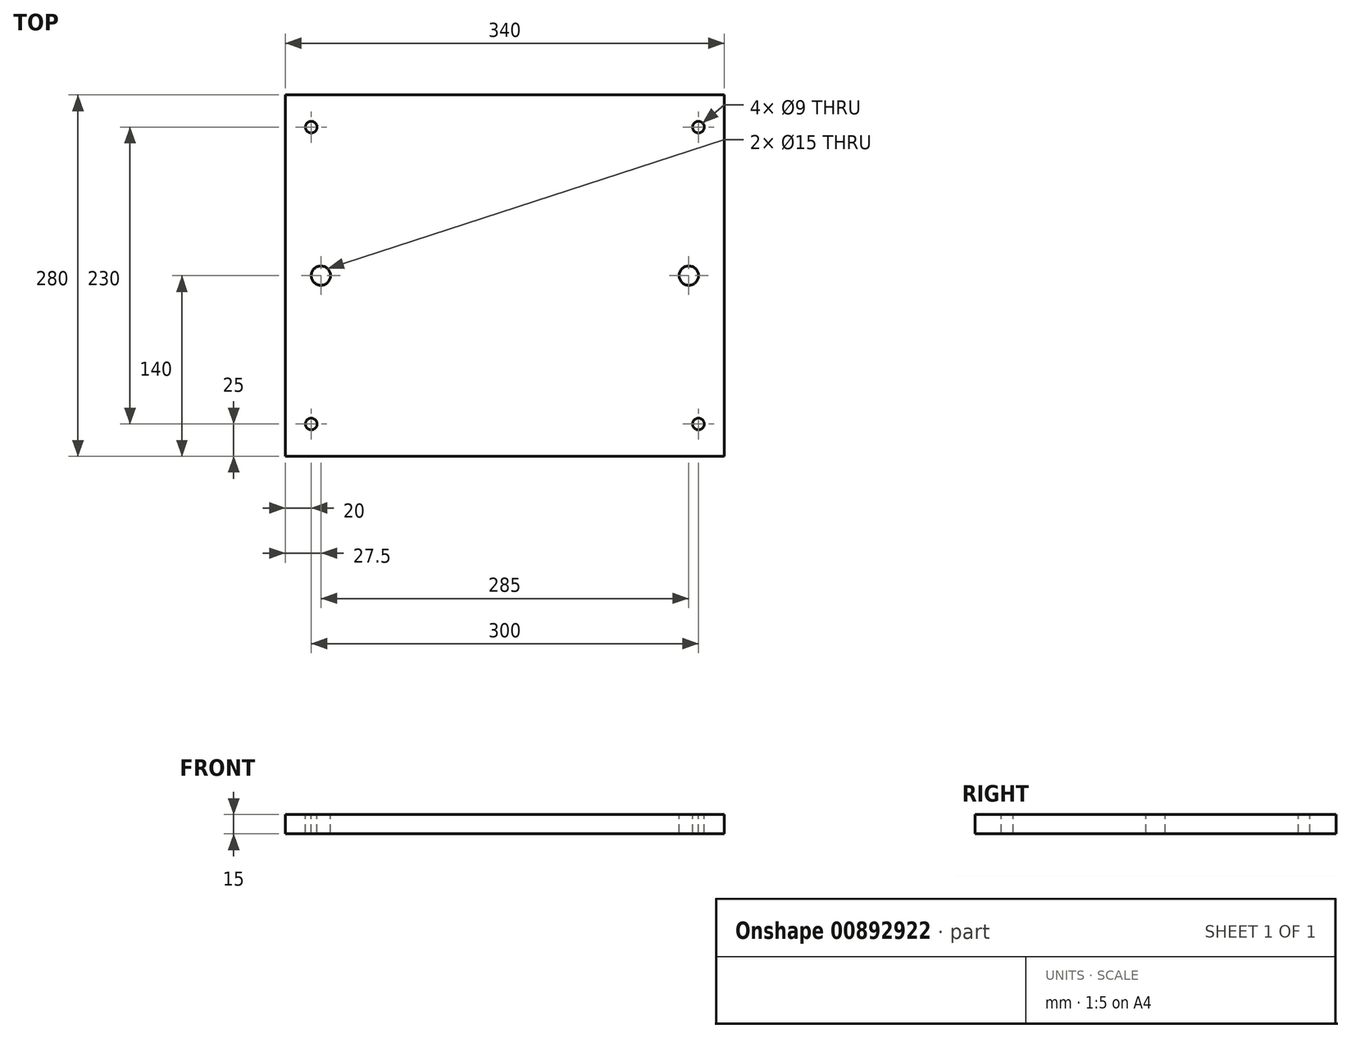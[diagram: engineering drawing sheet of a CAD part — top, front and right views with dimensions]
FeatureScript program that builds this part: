
annotation { "Feature Type Name" : "Feature", "Feature Type Description" : "" }
export const myFeature = defineFeature(function(context is Context, id is Id, definition is map)
    precondition{}
    {
        {
            var Q0;
            Q0=qCreatedBy(makeId("Top.planeOp"),FACE);
            var sketch = newSketch(context, id + "F0", { "sketchPlane" : qUnion([Q0])});
            skLineSegment(sketch, "E0.bottom", {"start": v(-170, 140) * mm, "end": v(170, 140) * mm});
            skLineSegment(sketch, "E0.top", {"start": v(-170, -140) * mm, "end": v(170, -140) * mm});
            skLineSegment(sketch, "E0.left", {"start": v(-170, 140) * mm, "end": v(-170, -140) * mm});
            skLineSegment(sketch, "E0.right", {"start": v(170, 140) * mm, "end": v(170, -140) * mm});
            skSolve(sketch);
        }
        {
            var Q0;
            Q0 = qSketchRegion(id + "F0", true);
            extrude(context, id + "F1", {"entities" : qUnion([Q0]), "depth" : 15 * mm, "offsetDistance" : 25 * mm});
        }
        {
            var Q0;
            Q0=makeQuery(id+"F1.opExtrude","CAP_FACE",FACE,{"disambiguationData":[OSD([sQuery(id+"F0.wireOp",EDGE,"E0.bottom"),sQuery(id+"F0.wireOp",EDGE,"E0.top"),sQuery(id+"F0.wireOp",EDGE,"E0.left"),sQuery(id+"F0.wireOp",EDGE,"E0.right")])],"isStart":false});
            var sketch = newSketch(context, id + "F2", { "sketchPlane" : qUnion([Q0])});
            skLineSegment(sketch, "E1", {"start": v(0, 140) * mm, "end": v(0, -140) * mm, "construction": true});
            skLineSegment(sketch, "E2", {"start": v(-170, 57.5) * mm, "end": v(170, 57.5) * mm, "construction": true});
            skLineSegment(sketch, "E3", {"start": v(-170, -57.5) * mm, "end": v(170, -57.5) * mm, "construction": true});
            skLineSegment(sketch, "E4", {"start": v(-150, 140) * mm, "end": v(-150, -140) * mm, "construction": true});
            skLineSegment(sketch, "E5", {"start": v(150, 140) * mm, "end": v(150, -140) * mm, "construction": true});
            skPoint(sketch, "E6", {"position": v(-150, -115) * mm});
            skPoint(sketch, "E7", {"position": v(-150, 115) * mm});
            skLineSegment(sketch, "E8", {"start": v(142.5, 0) * mm, "end": v(-142.5, 0) * mm, "construction": true});
            skPoint(sketch, "E9.MirrorP", {"position": v(150, -115) * mm});
            skPoint(sketch, "E10.MirrorP", {"position": v(150, 115) * mm});
            skPoint(sketch, "E11", {"position": v(-142.5, 0) * mm});
            skPoint(sketch, "E12", {"position": v(142.5, 0) * mm});
            skPoint(sketch, "E13", {"position": v(-150, 0) * mm});
            skSolve(sketch);
        }
        {
            var Q0;
            Q0=sQuery(id+"F2.wireOp",VERTEX,"E7");
            var Q1;
            Q1=sQuery(id+"F2.wireOp",VERTEX,"E6");
            var Q2;
            Q2=sQuery(id+"F2.wireOp",VERTEX,"E9.MirrorP");
            var Q3;
            Q3=sQuery(id+"F2.wireOp",VERTEX,"E10.MirrorP");
            var Q4;
            Q4=makeQuery(id+"F1.opExtrude","SWEPT_BODY",BODY,{"disambiguationData":[OSD([sQuery(id+"F0.wireOp",EDGE,"E0.bottom"),sQuery(id+"F0.wireOp",EDGE,"E0.top"),sQuery(id+"F0.wireOp",EDGE,"E0.left"),sQuery(id+"F0.wireOp",EDGE,"E0.right")])]});
            hole(context, id + "F3", {"style" : HoleStyle.SIMPLE, "endStyle" : HoleEndStyle.THROUGH, "holeDiameter" : 9 * mm, "majorDiameter" : 5 * mm, "isTappedThrough" : true, "tappedDepth" : 12.7 * mm, "tapClearance" : 3, "locations" : qUnion([Q0, Q1, Q2, Q3]), "scope" : qUnion([Q4])});
        }
        {
            var Q0;
            Q0=sQuery(id+"F2.wireOp",VERTEX,"E12");
            var Q1;
            Q1=sQuery(id+"F2.wireOp",VERTEX,"E11");
            var Q2;
            Q2=makeQuery(id+"F1.opExtrude","SWEPT_BODY",BODY,{"disambiguationData":[OSD([sQuery(id+"F0.wireOp",EDGE,"E0.bottom"),sQuery(id+"F0.wireOp",EDGE,"E0.top"),sQuery(id+"F0.wireOp",EDGE,"E0.left"),sQuery(id+"F0.wireOp",EDGE,"E0.right")])]});
            hole(context, id + "F4", {"style" : HoleStyle.SIMPLE, "endStyle" : HoleEndStyle.THROUGH, "holeDiameter" : 15 * mm, "majorDiameter" : 5 * mm, "isTappedThrough" : true, "tappedDepth" : 12.7 * mm, "tapClearance" : 3, "locations" : qUnion([Q0, Q1]), "scope" : qUnion([Q2])});
        }
    });
